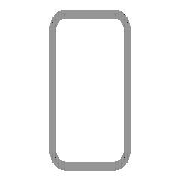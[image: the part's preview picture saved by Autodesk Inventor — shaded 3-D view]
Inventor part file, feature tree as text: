
AUTODESK INVENTOR PART (.ipt)
format: ipt  version: 2025 (Build 290162010, 162A)  size: 129,024 bytes
history: native  units: mm (DEFAULTED — no unit token found)
features: other x3, sketch x1, plane x1
ambient origin geometry x8: Origin, YZ Plane, XZ Plane, XY Plane, X Axis, Y Axis, Z Axis, Center Point
bodies: Solid1 (feature_tree), Body (feature_tree)
feature tree (5):
  other  "Driven Length"
  other  "Start plane"
  other  "End plane"
  sketch  "Sketch3"  dims[d3=1090.0mm d4=0.0mm d7=4.0mm d9=40.0mm d11=80.0mm d12=2.0mm d13=-0.0mm d14=1090.0mm d15=20.0mm d16=40.0mm d17=90.0deg d18=1090.0mm]
  plane  "Work Plane3"
